# Revit family: opening bi folding shutterdoor
name_source: partatom
category: Doors
revit_build: Autodesk Revit 2014 (Build: 20130722_2115(x64)
units: mm (PartAtom-declared; Revit-internal decimal feet)

## types (5) — shared parameters
Analytic Construction = <None>
Construction Details = http://www.arcat.com
Description = LaCantina Wood Series Folding Door System as Specified
E1996_Large-Missile-Impact = Contact LaCantina for information
Fire Rating = As Specified
Frame Thickness = 143 mm
Jamb Thickness_Sides = 32 mm
Jamb Thickness_Top = 57 mm
Keynote = 08350
Manufacturer = LaCantina Doors, Inc.
Manufacturer Fax = 760-734- 1591
Manufacturer Website = http://www.lacantinadoors.com
Max Height = 3150 mm
Model = Wood Series
Product Data = http://www.arcat.com
RO Spacing Sides = 13 mm  [stored 0.0426509 ft]
RO Spacing Top = 19 mm
Sales Information = http://www.lacantinadoors.com
Send Message = http://www.arcat.com
Slab Inset from Edge of Frame = 51 mm
Specification = http://www.arcat.com
URL = http://www.lacantinadoors.com
zero-valued in all types: Expected Lifespan (Years), Maintenance Schedule (Months), SHGC, U-Factor, Visible Light Transmission, Warranty Duration (Years)

## per-type parameters (varying)
| type | Air Space Below Door | E283_Air-Infiltration | E330_Structural-Test-Pressure | E547_Water-Resistance | Function | Max Width | Sill Height | Thickness | Threshold Type | Wall Closure | sill_adaramp | sill_flushguide | sill_weatherresist | sill_zerostep |
| Weather Resistant Sill | 10 mm  [stored 0.0328084 ft] | 0.11 CFM/ft^2 tested at 1.57 psf (25 MPH) | Deflection +0.851" / -0.963" tested at 25 DP | No leakage tested at 4.5 psf | Exterior | 30000 mm | 24 mm | 550 mm | Sill : Weather Resistant | Both | No | No | Yes | No |
| Flush Guide Sill | 8 mm  [stored 0.0262467 ft] | Contact LaCantina for information | Contact LaCantina for information | Contact LaCantina for information | Interior | 19812 mm | 0 mm  [stored 0 ft] | 0 mm  [stored 0 ft] | Sill : Flush Guide | By host | No | Yes | No | No |
| ADA Ramp Sill | 8 mm  [stored 0.0262467 ft] | Contact LaCantina for information | Contact LaCantina for information | Contact LaCantina for information | Interior | 19812 mm | 13 mm  [stored 0.0426509 ft] | 0 mm  [stored 0 ft] | Sill : ADA Ramp | By host | Yes | No | No | No |
| Zero Step Sill | 8 mm  [stored 0.0262467 ft] | Contact LaCantina for information | Contact LaCantina for information | Contact LaCantina for information | Interior | 10000 mm | 0 mm  [stored 0 ft] | 0 mm  [stored 0 ft] | Sill : Zero Step | By host | No | No | No | Yes |
| Weather Resistant Sill 2 smaller | 10 mm  [stored 0.0328084 ft] | 0.11 CFM/ft^2 tested at 1.57 psf (25 MPH) | Deflection +0.851" / -0.963" tested at 25 DP | No leakage tested at 4.5 psf | Exterior | 30000 mm | 24 mm | 550 mm | Sill : Weather Resistant | Both | No | No | Yes | No |

note: [stored X ft] marks values corroborated as IEEE doubles in the binary element streams (Revit-internal decimal feet)

## geometry (parser evidence)
native form markers: Blend x2, Sweep x15
no freeform markers — native parametric forms only
